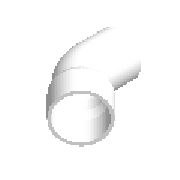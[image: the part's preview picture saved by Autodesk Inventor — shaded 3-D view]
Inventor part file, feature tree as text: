
AUTODESK INVENTOR PART (.ipt)
format: ipt  version: 2024.2 (Build 282272000, 272)  size: 217,088 bytes
history: native  units: mm (DEFAULTED — no unit token found)
features: other x4, revolve x1
ambient origin geometry x8: Origin, YZ Plane, XZ Plane, XY Plane, X Axis, Y Axis, Z Axis, Center Point
bodies: Solid1 (feature_tree)
feature tree (5):
  revolve  "Revolution1"  [1 undecoded]
  other  "Work Axis30"
  other  "Work Point19"
  other  "Work Axis31"
  other  "Work Point20"
note: 1 required parameter value undecoded (feature->parameter linkage not recoverable at this tier; creation-order binding heuristic only, values carry confidence <= 0.55)
